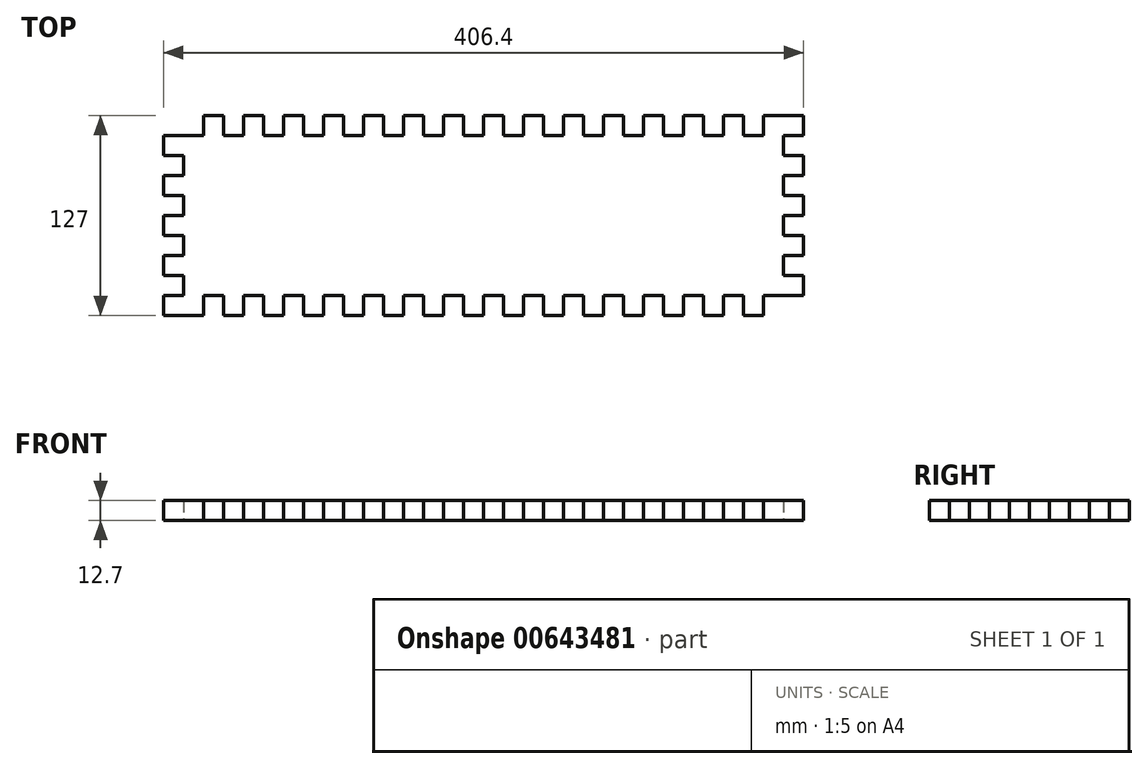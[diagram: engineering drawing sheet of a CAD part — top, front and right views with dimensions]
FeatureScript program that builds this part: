
annotation { "Feature Type Name" : "Feature", "Feature Type Description" : "" }
export const myFeature = defineFeature(function(context is Context, id is Id, definition is map)
    precondition{}
    {
        {
            var Q0;
            Q0=qCreatedBy(makeId("Top.planeOp"),FACE);
            var sketch = newSketch(context, id + "F0", { "sketchPlane" : qUnion([Q0])});
            skLineSegment(sketch, "E0.bottom", {"start": v(-138.01, 68.75) * mm, "end": v(242.99, 68.75) * mm});
            skLineSegment(sketch, "E0.top", {"start": v(-138.01, -58.25) * mm, "end": v(242.99, -58.25) * mm});
            skLineSegment(sketch, "E0.left", {"start": v(-138.01, 68.75) * mm, "end": v(-138.01, -58.25) * mm});
            skLineSegment(sketch, "E0.right", {"start": v(242.99, 68.75) * mm, "end": v(242.99, -58.25) * mm});
            skLineSegment(sketch, "E1.bottom", {"start": v(-125.31, 68.75) * mm, "end": v(-112.61, 68.75) * mm});
            skLineSegment(sketch, "E1.left", {"start": v(-125.31, 68.75) * mm, "end": v(-125.31, 56.05) * mm});
            skLineSegment(sketch, "E1.right", {"start": v(-112.61, 68.75) * mm, "end": v(-112.61, 56.05) * mm});
            skLineSegment(sketch, "E2.bottom", {"start": v(141.39, 68.75) * mm, "end": v(192.19, 68.75) * mm});
            skLineSegment(sketch, "E2.left", {"start": v(141.39, 68.75) * mm, "end": v(141.39, 56.05) * mm});
            skLineSegment(sketch, "E2.right", {"start": v(192.19, 68.75) * mm, "end": v(192.19, 56.05) * mm});
            skLineSegment(sketch, "E3.bottom", {"start": v(-125.31, -58.25) * mm, "end": v(-112.61, -58.25) * mm});
            skLineSegment(sketch, "E3.top", {"start": v(-125.31, -45.55) * mm, "end": v(-112.61, -45.55) * mm});
            skLineSegment(sketch, "E3.left", {"start": v(-125.31, -58.25) * mm, "end": v(-125.31, -45.55) * mm});
            skLineSegment(sketch, "E3.right", {"start": v(-112.61, -58.25) * mm, "end": v(-112.61, -45.55) * mm});
            skLineSegment(sketch, "E4.bottom", {"start": v(204.89, -58.25) * mm, "end": v(217.59, -58.25) * mm});
            skLineSegment(sketch, "E4.top", {"start": v(204.89, -45.55) * mm, "end": v(217.59, -45.55) * mm});
            skLineSegment(sketch, "E4.left", {"start": v(204.89, -58.25) * mm, "end": v(204.89, -45.55) * mm});
            skLineSegment(sketch, "E4.right", {"start": v(217.59, -58.25) * mm, "end": v(217.59, -45.55) * mm});
            skLineSegment(sketch, "E5.left", {"start": v(242.99, 68.75) * mm, "end": v(242.99, 30.65) * mm});
            skLineSegment(sketch, "E6.left", {"start": v(242.99, -58.25) * mm, "end": v(242.99, -20.15) * mm});
            skLineSegment(sketch, "E7.left", {"start": v(-138.01, 68.75) * mm, "end": v(-138.01, 30.65) * mm});
            skLineSegment(sketch, "E8.bottom", {"start": v(-138.01, -58.25) * mm, "end": v(-150.71, -58.25) * mm});
            skLineSegment(sketch, "E8.top", {"start": v(-138.01, -45.55) * mm, "end": v(-150.71, -45.55) * mm});
            skLineSegment(sketch, "E8.left", {"start": v(-138.01, -58.25) * mm, "end": v(-138.01, -45.55) * mm});
            skLineSegment(sketch, "E8.right", {"start": v(-150.71, -58.25) * mm, "end": v(-150.71, -45.55) * mm});
            skLineSegment(sketch, "E9.bottom", {"start": v(-99.91, -45.55) * mm, "end": v(-87.21, -45.55) * mm});
            skLineSegment(sketch, "E9.top", {"start": v(-99.91, -58.25) * mm, "end": v(-87.21, -58.25) * mm});
            skLineSegment(sketch, "E9.left", {"start": v(-99.91, -45.55) * mm, "end": v(-99.91, -58.25) * mm});
            skLineSegment(sketch, "E9.right", {"start": v(-87.21, -45.55) * mm, "end": v(-87.21, -58.25) * mm});
            skLineSegment(sketch, "E10.bottom", {"start": v(-74.51, -45.55) * mm, "end": v(-61.81, -45.55) * mm});
            skLineSegment(sketch, "E10.top", {"start": v(-74.51, -58.25) * mm, "end": v(-61.81, -58.25) * mm});
            skLineSegment(sketch, "E10.left", {"start": v(-74.51, -45.55) * mm, "end": v(-74.51, -58.25) * mm});
            skLineSegment(sketch, "E10.right", {"start": v(-61.81, -45.55) * mm, "end": v(-61.81, -58.25) * mm});
            skLineSegment(sketch, "E11.bottom", {"start": v(-49.11, -45.55) * mm, "end": v(-36.41, -45.55) * mm});
            skLineSegment(sketch, "E11.top", {"start": v(-49.11, -58.25) * mm, "end": v(-36.41, -58.25) * mm});
            skLineSegment(sketch, "E11.left", {"start": v(-49.11, -45.55) * mm, "end": v(-49.11, -58.25) * mm});
            skLineSegment(sketch, "E11.right", {"start": v(-36.41, -45.55) * mm, "end": v(-36.41, -58.25) * mm});
            skLineSegment(sketch, "E12.bottom", {"start": v(-23.71, -45.55) * mm, "end": v(-11.01, -45.55) * mm});
            skLineSegment(sketch, "E12.top", {"start": v(-23.71, -58.25) * mm, "end": v(-11.01, -58.25) * mm});
            skLineSegment(sketch, "E12.left", {"start": v(-23.71, -45.55) * mm, "end": v(-23.71, -58.25) * mm});
            skLineSegment(sketch, "E12.right", {"start": v(-11.01, -45.55) * mm, "end": v(-11.01, -58.25) * mm});
            skLineSegment(sketch, "E13.bottom", {"start": v(1.69, -45.55) * mm, "end": v(14.39, -45.55) * mm});
            skLineSegment(sketch, "E13.top", {"start": v(1.69, -58.25) * mm, "end": v(14.39, -58.25) * mm});
            skLineSegment(sketch, "E13.left", {"start": v(1.69, -45.55) * mm, "end": v(1.69, -58.25) * mm});
            skLineSegment(sketch, "E13.right", {"start": v(14.39, -45.55) * mm, "end": v(14.39, -58.25) * mm});
            skLineSegment(sketch, "E14.bottom", {"start": v(27.09, -58.25) * mm, "end": v(39.79, -58.25) * mm});
            skLineSegment(sketch, "E14.top", {"start": v(27.09, -45.55) * mm, "end": v(39.79, -45.55) * mm});
            skLineSegment(sketch, "E14.left", {"start": v(27.09, -58.25) * mm, "end": v(27.09, -45.55) * mm});
            skLineSegment(sketch, "E14.right", {"start": v(39.79, -58.25) * mm, "end": v(39.79, -45.55) * mm});
            skLineSegment(sketch, "E15.bottom", {"start": v(52.49, -58.25) * mm, "end": v(65.19, -58.25) * mm});
            skLineSegment(sketch, "E15.top", {"start": v(52.49, -45.55) * mm, "end": v(65.19, -45.55) * mm});
            skLineSegment(sketch, "E15.left", {"start": v(52.49, -58.25) * mm, "end": v(52.49, -45.55) * mm});
            skLineSegment(sketch, "E15.right", {"start": v(65.19, -58.25) * mm, "end": v(65.19, -45.55) * mm});
            skLineSegment(sketch, "E16.bottom", {"start": v(77.89, -58.25) * mm, "end": v(90.59, -58.25) * mm});
            skLineSegment(sketch, "E16.top", {"start": v(77.89, -45.55) * mm, "end": v(90.59, -45.55) * mm});
            skLineSegment(sketch, "E16.left", {"start": v(77.89, -58.25) * mm, "end": v(77.89, -45.55) * mm});
            skLineSegment(sketch, "E16.right", {"start": v(90.59, -58.25) * mm, "end": v(90.59, -45.55) * mm});
            skLineSegment(sketch, "E17.bottom", {"start": v(103.29, -58.25) * mm, "end": v(115.99, -58.25) * mm});
            skLineSegment(sketch, "E17.top", {"start": v(103.29, -45.55) * mm, "end": v(115.99, -45.55) * mm});
            skLineSegment(sketch, "E17.left", {"start": v(103.29, -58.25) * mm, "end": v(103.29, -45.55) * mm});
            skLineSegment(sketch, "E17.right", {"start": v(115.99, -58.25) * mm, "end": v(115.99, -45.55) * mm});
            skLineSegment(sketch, "E18.bottom", {"start": v(128.69, -58.25) * mm, "end": v(141.39, -58.25) * mm});
            skLineSegment(sketch, "E18.top", {"start": v(128.69, -45.55) * mm, "end": v(141.39, -45.55) * mm});
            skLineSegment(sketch, "E18.left", {"start": v(128.69, -58.25) * mm, "end": v(128.69, -45.55) * mm});
            skLineSegment(sketch, "E18.right", {"start": v(141.39, -58.25) * mm, "end": v(141.39, -45.55) * mm});
            skLineSegment(sketch, "E19.bottom", {"start": v(154.09, -58.25) * mm, "end": v(166.79, -58.25) * mm});
            skLineSegment(sketch, "E19.top", {"start": v(154.09, -45.55) * mm, "end": v(166.79, -45.55) * mm});
            skLineSegment(sketch, "E19.left", {"start": v(154.09, -58.25) * mm, "end": v(154.09, -45.55) * mm});
            skLineSegment(sketch, "E19.right", {"start": v(166.79, -58.25) * mm, "end": v(166.79, -45.55) * mm});
            skLineSegment(sketch, "E20.bottom", {"start": v(179.49, -58.25) * mm, "end": v(192.19, -58.25) * mm});
            skLineSegment(sketch, "E20.top", {"start": v(179.49, -45.55) * mm, "end": v(192.19, -45.55) * mm});
            skLineSegment(sketch, "E20.left", {"start": v(179.49, -58.25) * mm, "end": v(179.49, -45.55) * mm});
            skLineSegment(sketch, "E20.right", {"start": v(192.19, -58.25) * mm, "end": v(192.19, -45.55) * mm});
            skLineSegment(sketch, "E21.bottom", {"start": v(242.99, -58.25) * mm, "end": v(230.29, -58.25) * mm});
            skLineSegment(sketch, "E21.top", {"start": v(242.99, -45.55) * mm, "end": v(230.29, -45.55) * mm});
            skLineSegment(sketch, "E21.left", {"start": v(242.99, -58.25) * mm, "end": v(242.99, -45.55) * mm});
            skLineSegment(sketch, "E21.right", {"start": v(230.29, -58.25) * mm, "end": v(230.29, -45.55) * mm});
            skLineSegment(sketch, "E22.bottom", {"start": v(-112.61, 56.05) * mm, "end": v(-99.91, 56.05) * mm});
            skLineSegment(sketch, "E22.top", {"start": v(-112.61, 68.75) * mm, "end": v(-99.91, 68.75) * mm});
            skLineSegment(sketch, "E22.left", {"start": v(-112.61, 56.05) * mm, "end": v(-112.61, 68.75) * mm});
            skLineSegment(sketch, "E22.right", {"start": v(-99.91, 56.05) * mm, "end": v(-99.91, 68.75) * mm});
            skLineSegment(sketch, "E23.bottom", {"start": v(217.59, 56.05) * mm, "end": v(230.29, 56.05) * mm});
            skLineSegment(sketch, "E23.top", {"start": v(217.59, 68.75) * mm, "end": v(230.29, 68.75) * mm});
            skLineSegment(sketch, "E23.left", {"start": v(217.59, 56.05) * mm, "end": v(217.59, 68.75) * mm});
            skLineSegment(sketch, "E23.right", {"start": v(230.29, 56.05) * mm, "end": v(230.29, 68.75) * mm});
            skLineSegment(sketch, "E24.bottom", {"start": v(-125.31, 56.05) * mm, "end": v(-138.01, 56.05) * mm});
            skLineSegment(sketch, "E24.top", {"start": v(-125.31, 68.75) * mm, "end": v(-138.01, 68.75) * mm});
            skLineSegment(sketch, "E24.left", {"start": v(-125.31, 56.05) * mm, "end": v(-125.31, 68.75) * mm});
            skLineSegment(sketch, "E24.right", {"start": v(-138.01, 56.05) * mm, "end": v(-138.01, 68.75) * mm});
            skLineSegment(sketch, "E25.bottom", {"start": v(-87.21, 68.75) * mm, "end": v(-74.51, 68.75) * mm});
            skLineSegment(sketch, "E25.top", {"start": v(-87.21, 56.05) * mm, "end": v(-74.51, 56.05) * mm});
            skLineSegment(sketch, "E25.left", {"start": v(-87.21, 68.75) * mm, "end": v(-87.21, 56.05) * mm});
            skLineSegment(sketch, "E25.right", {"start": v(-74.51, 68.75) * mm, "end": v(-74.51, 56.05) * mm});
            skLineSegment(sketch, "E26.bottom", {"start": v(-61.81, 68.75) * mm, "end": v(-49.11, 68.75) * mm});
            skLineSegment(sketch, "E26.top", {"start": v(-61.81, 56.05) * mm, "end": v(-49.11, 56.05) * mm});
            skLineSegment(sketch, "E26.left", {"start": v(-61.81, 68.75) * mm, "end": v(-61.81, 56.05) * mm});
            skLineSegment(sketch, "E26.right", {"start": v(-49.11, 68.75) * mm, "end": v(-49.11, 56.05) * mm});
            skLineSegment(sketch, "E27.bottom", {"start": v(-36.41, 68.75) * mm, "end": v(-23.71, 68.75) * mm});
            skLineSegment(sketch, "E27.top", {"start": v(-36.41, 56.05) * mm, "end": v(-23.71, 56.05) * mm});
            skLineSegment(sketch, "E27.left", {"start": v(-36.41, 68.75) * mm, "end": v(-36.41, 56.05) * mm});
            skLineSegment(sketch, "E27.right", {"start": v(-23.71, 68.75) * mm, "end": v(-23.71, 56.05) * mm});
            skLineSegment(sketch, "E28.bottom", {"start": v(-11.01, 68.75) * mm, "end": v(1.69, 68.75) * mm});
            skLineSegment(sketch, "E28.top", {"start": v(-11.01, 56.05) * mm, "end": v(1.69, 56.05) * mm});
            skLineSegment(sketch, "E28.left", {"start": v(-11.01, 68.75) * mm, "end": v(-11.01, 56.05) * mm});
            skLineSegment(sketch, "E28.right", {"start": v(1.69, 68.75) * mm, "end": v(1.69, 56.05) * mm});
            skLineSegment(sketch, "E29.bottom", {"start": v(14.39, 68.75) * mm, "end": v(27.09, 68.75) * mm});
            skLineSegment(sketch, "E29.top", {"start": v(14.39, 56.05) * mm, "end": v(27.09, 56.05) * mm});
            skLineSegment(sketch, "E29.left", {"start": v(14.39, 68.75) * mm, "end": v(14.39, 56.05) * mm});
            skLineSegment(sketch, "E29.right", {"start": v(27.09, 68.75) * mm, "end": v(27.09, 56.05) * mm});
            skLineSegment(sketch, "E30.bottom", {"start": v(39.79, 56.05) * mm, "end": v(52.49, 56.05) * mm});
            skLineSegment(sketch, "E30.top", {"start": v(39.79, 68.75) * mm, "end": v(52.49, 68.75) * mm});
            skLineSegment(sketch, "E30.left", {"start": v(39.79, 56.05) * mm, "end": v(39.79, 68.75) * mm});
            skLineSegment(sketch, "E30.right", {"start": v(52.49, 56.05) * mm, "end": v(52.49, 68.75) * mm});
            skLineSegment(sketch, "E31.bottom", {"start": v(65.19, 56.05) * mm, "end": v(77.89, 56.05) * mm});
            skLineSegment(sketch, "E31.top", {"start": v(65.19, 68.75) * mm, "end": v(77.89, 68.75) * mm});
            skLineSegment(sketch, "E31.left", {"start": v(65.19, 56.05) * mm, "end": v(65.19, 68.75) * mm});
            skLineSegment(sketch, "E31.right", {"start": v(77.89, 56.05) * mm, "end": v(77.89, 68.75) * mm});
            skLineSegment(sketch, "E32.bottom", {"start": v(90.59, 56.05) * mm, "end": v(103.29, 56.05) * mm});
            skLineSegment(sketch, "E32.top", {"start": v(90.59, 68.75) * mm, "end": v(103.29, 68.75) * mm});
            skLineSegment(sketch, "E32.left", {"start": v(90.59, 56.05) * mm, "end": v(90.59, 68.75) * mm});
            skLineSegment(sketch, "E32.right", {"start": v(103.29, 56.05) * mm, "end": v(103.29, 68.75) * mm});
            skLineSegment(sketch, "E33.bottom", {"start": v(115.99, 56.05) * mm, "end": v(128.69, 56.05) * mm});
            skLineSegment(sketch, "E33.top", {"start": v(115.99, 68.75) * mm, "end": v(128.69, 68.75) * mm});
            skLineSegment(sketch, "E33.left", {"start": v(115.99, 56.05) * mm, "end": v(115.99, 68.75) * mm});
            skLineSegment(sketch, "E33.right", {"start": v(128.69, 56.05) * mm, "end": v(128.69, 68.75) * mm});
            skLineSegment(sketch, "E34.bottom", {"start": v(141.39, 56.05) * mm, "end": v(154.09, 56.05) * mm});
            skLineSegment(sketch, "E34.top", {"start": v(141.39, 68.75) * mm, "end": v(154.09, 68.75) * mm});
            skLineSegment(sketch, "E34.left", {"start": v(141.39, 56.05) * mm, "end": v(141.39, 68.75) * mm});
            skLineSegment(sketch, "E34.right", {"start": v(154.09, 56.05) * mm, "end": v(154.09, 68.75) * mm});
            skLineSegment(sketch, "E35.bottom", {"start": v(166.79, 56.05) * mm, "end": v(179.49, 56.05) * mm});
            skLineSegment(sketch, "E35.top", {"start": v(166.79, 68.75) * mm, "end": v(179.49, 68.75) * mm});
            skLineSegment(sketch, "E35.left", {"start": v(166.79, 56.05) * mm, "end": v(166.79, 68.75) * mm});
            skLineSegment(sketch, "E35.right", {"start": v(179.49, 56.05) * mm, "end": v(179.49, 68.75) * mm});
            skLineSegment(sketch, "E36.bottom", {"start": v(192.19, 56.05) * mm, "end": v(204.89, 56.05) * mm});
            skLineSegment(sketch, "E36.top", {"start": v(192.19, 68.75) * mm, "end": v(204.89, 68.75) * mm});
            skLineSegment(sketch, "E36.left", {"start": v(192.19, 56.05) * mm, "end": v(192.19, 68.75) * mm});
            skLineSegment(sketch, "E36.right", {"start": v(204.89, 56.05) * mm, "end": v(204.89, 68.75) * mm});
            skLineSegment(sketch, "E37.right", {"start": v(242.99, 56.05) * mm, "end": v(242.99, 68.75) * mm});
            skLineSegment(sketch, "E38.bottom", {"start": v(-138.01, 30.65) * mm, "end": v(-150.71, 30.65) * mm});
            skLineSegment(sketch, "E38.top", {"start": v(-138.01, 17.95) * mm, "end": v(-150.71, 17.95) * mm});
            skLineSegment(sketch, "E38.left", {"start": v(-138.01, 30.65) * mm, "end": v(-138.01, 17.95) * mm});
            skLineSegment(sketch, "E38.right", {"start": v(-150.71, 30.65) * mm, "end": v(-150.71, 17.95) * mm});
            skLineSegment(sketch, "E39.bottom", {"start": v(-138.01, 5.25) * mm, "end": v(-150.71, 5.25) * mm});
            skLineSegment(sketch, "E39.top", {"start": v(-138.01, -7.45) * mm, "end": v(-150.71, -7.45) * mm});
            skLineSegment(sketch, "E39.left", {"start": v(-138.01, 5.25) * mm, "end": v(-138.01, -7.45) * mm});
            skLineSegment(sketch, "E39.right", {"start": v(-150.71, 5.25) * mm, "end": v(-150.71, -7.45) * mm});
            skLineSegment(sketch, "E40.bottom", {"start": v(-138.01, -20.15) * mm, "end": v(-150.71, -20.15) * mm});
            skLineSegment(sketch, "E40.top", {"start": v(-138.01, -32.85) * mm, "end": v(-150.71, -32.85) * mm});
            skLineSegment(sketch, "E40.left", {"start": v(-138.01, -20.15) * mm, "end": v(-138.01, -32.85) * mm});
            skLineSegment(sketch, "E40.right", {"start": v(-150.71, -20.15) * mm, "end": v(-150.71, -32.85) * mm});
            skLineSegment(sketch, "E41.bottom", {"start": v(-150.71, 56.05) * mm, "end": v(-138.01, 56.05) * mm});
            skLineSegment(sketch, "E41.top", {"start": v(-150.71, 43.35) * mm, "end": v(-138.01, 43.35) * mm});
            skLineSegment(sketch, "E41.left", {"start": v(-150.71, 56.05) * mm, "end": v(-150.71, 43.35) * mm});
            skLineSegment(sketch, "E41.right", {"start": v(-138.01, 56.05) * mm, "end": v(-138.01, 43.35) * mm});
            skLineSegment(sketch, "E42.bottom", {"start": v(255.69, -45.55) * mm, "end": v(242.99, -45.55) * mm});
            skLineSegment(sketch, "E42.top", {"start": v(255.69, -32.85) * mm, "end": v(242.99, -32.85) * mm});
            skLineSegment(sketch, "E42.left", {"start": v(255.69, -45.55) * mm, "end": v(255.69, -32.85) * mm});
            skLineSegment(sketch, "E42.right", {"start": v(242.99, -45.55) * mm, "end": v(242.99, -32.85) * mm});
            skLineSegment(sketch, "E43.bottom", {"start": v(255.69, 43.35) * mm, "end": v(242.99, 43.35) * mm});
            skLineSegment(sketch, "E43.top", {"start": v(255.69, 30.65) * mm, "end": v(242.99, 30.65) * mm});
            skLineSegment(sketch, "E43.left", {"start": v(255.69, 43.35) * mm, "end": v(255.69, 30.65) * mm});
            skLineSegment(sketch, "E43.right", {"start": v(242.99, 43.35) * mm, "end": v(242.99, 30.65) * mm});
            skLineSegment(sketch, "E44.bottom", {"start": v(255.69, 17.95) * mm, "end": v(242.99, 17.95) * mm});
            skLineSegment(sketch, "E44.top", {"start": v(255.69, 5.25) * mm, "end": v(242.99, 5.25) * mm});
            skLineSegment(sketch, "E44.left", {"start": v(255.69, 17.95) * mm, "end": v(255.69, 5.25) * mm});
            skLineSegment(sketch, "E44.right", {"start": v(242.99, 17.95) * mm, "end": v(242.99, 5.25) * mm});
            skLineSegment(sketch, "E45.bottom", {"start": v(255.69, -7.45) * mm, "end": v(242.99, -7.45) * mm});
            skLineSegment(sketch, "E45.top", {"start": v(255.69, -20.15) * mm, "end": v(242.99, -20.15) * mm});
            skLineSegment(sketch, "E45.left", {"start": v(255.69, -7.45) * mm, "end": v(255.69, -20.15) * mm});
            skLineSegment(sketch, "E45.right", {"start": v(242.99, -7.45) * mm, "end": v(242.99, -20.15) * mm});
            skLineSegment(sketch, "E46.bottom", {"start": v(242.99, 68.75) * mm, "end": v(255.69, 68.75) * mm});
            skLineSegment(sketch, "E46.top", {"start": v(242.99, 56.05) * mm, "end": v(255.69, 56.05) * mm});
            skLineSegment(sketch, "E46.left", {"start": v(242.99, 68.75) * mm, "end": v(242.99, 56.05) * mm});
            skLineSegment(sketch, "E46.right", {"start": v(255.69, 68.75) * mm, "end": v(255.69, 56.05) * mm});
            skSolve(sketch);
        }
        {
            var Q0;
            Q0=makeQuery(id+"F0.imprint","IMPRINT",FACE,{"disambiguationData":[TD([[makeQuery(id+"F0.imprint","IMPRINT",EDGE,{"derivedFrom":sQuery(id+"F0.wireOp",EDGE,"E0.bottom")}),-1.0]])]});
            var Q1;
            Q1=makeQuery(id+"F0.imprint","IMPRINT",FACE,{"disambiguationData":[TD([[makeQuery(id+"F0.imprint","IMPRINT",EDGE,{"derivedFrom":sQuery(id+"F0.wireOp",EDGE,"E7.bottom")}),1.0]])]});
            var Q2;
            Q2=makeQuery(id+"F0.imprint","IMPRINT",FACE,{"disambiguationData":[TD([[makeQuery(id+"F0.imprint","IMPRINT",EDGE,{"derivedFrom":sQuery(id+"F0.wireOp",EDGE,"E8.bottom")}),-1.0]])]});
            var Q3;
            Q3=makeQuery(id+"F0.imprint","IMPRINT",FACE,{"disambiguationData":[TD([[makeQuery(id+"F0.imprint","IMPRINT",EDGE,{"derivedFrom":sQuery(id+"F0.wireOp",EDGE,"E5.bottom")}),-1.0]])]});
            var Q4;
            Q4=makeQuery(id+"F0.imprint","IMPRINT",FACE,{"disambiguationData":[TD([[makeQuery(id+"F0.imprint","IMPRINT",EDGE,{"derivedFrom":sQuery(id+"F0.wireOp",EDGE,"E6.bottom")}),1.0]])]});
            var Q5;
            Q5=makeQuery(id+"F0.imprint","IMPRINT",FACE,{"disambiguationData":[TD([[makeQuery(id+"F0.imprint","IMPRINT",EDGE,{"derivedFrom":sQuery(id+"F0.wireOp",EDGE,"E41.bottom")}),-1.0]])]});
            var Q6;
            Q6=makeQuery(id+"F0.imprint","IMPRINT",FACE,{"disambiguationData":[TD([[makeQuery(id+"F0.imprint","IMPRINT",EDGE,{"derivedFrom":sQuery(id+"F0.wireOp",EDGE,"E38.bottom")}),1.0]])]});
            var Q7;
            Q7=makeQuery(id+"F0.imprint","IMPRINT",FACE,{"disambiguationData":[TD([[makeQuery(id+"F0.imprint","IMPRINT",EDGE,{"derivedFrom":sQuery(id+"F0.wireOp",EDGE,"E39.bottom")}),1.0]])]});
            var Q8;
            Q8=makeQuery(id+"F0.imprint","IMPRINT",FACE,{"disambiguationData":[TD([[makeQuery(id+"F0.imprint","IMPRINT",EDGE,{"derivedFrom":sQuery(id+"F0.wireOp",EDGE,"E40.bottom")}),1.0]])]});
            var Q9;
            Q9=makeQuery(id+"F0.imprint","IMPRINT",FACE,{"disambiguationData":[TD([[makeQuery(id+"F0.imprint","IMPRINT",EDGE,{"derivedFrom":sQuery(id+"F0.wireOp",EDGE,"E42.bottom")}),-1.0]])]});
            var Q10;
            Q10=makeQuery(id+"F0.imprint","IMPRINT",FACE,{"disambiguationData":[TD([[makeQuery(id+"F0.imprint","IMPRINT",EDGE,{"derivedFrom":sQuery(id+"F0.wireOp",EDGE,"E45.bottom")}),1.0]])]});
            var Q11;
            Q11=makeQuery(id+"F0.imprint","IMPRINT",FACE,{"disambiguationData":[TD([[makeQuery(id+"F0.imprint","IMPRINT",EDGE,{"derivedFrom":sQuery(id+"F0.wireOp",EDGE,"E44.bottom")}),1.0]])]});
            var Q12;
            Q12=makeQuery(id+"F0.imprint","IMPRINT",FACE,{"disambiguationData":[TD([[makeQuery(id+"F0.imprint","IMPRINT",EDGE,{"derivedFrom":sQuery(id+"F0.wireOp",EDGE,"E43.bottom")}),1.0]])]});
            var Q13;
            Q13=makeQuery(id+"F0.imprint","IMPRINT",FACE,{"disambiguationData":[TD([[makeQuery(id+"F0.imprint","IMPRINT",EDGE,{"derivedFrom":sQuery(id+"F0.wireOp",EDGE,"E46.bottom")}),-1.0]])]});
            extrude(context, id + "F1", {"entities" : qUnion([Q0, Q1, Q2, Q3, Q4, Q5, Q6, Q7, Q8, Q9, Q10, Q11, Q12, Q13]), "depth" : 12.7 * mm, "offsetDistance" : 25.4 * mm});
        }
    });
